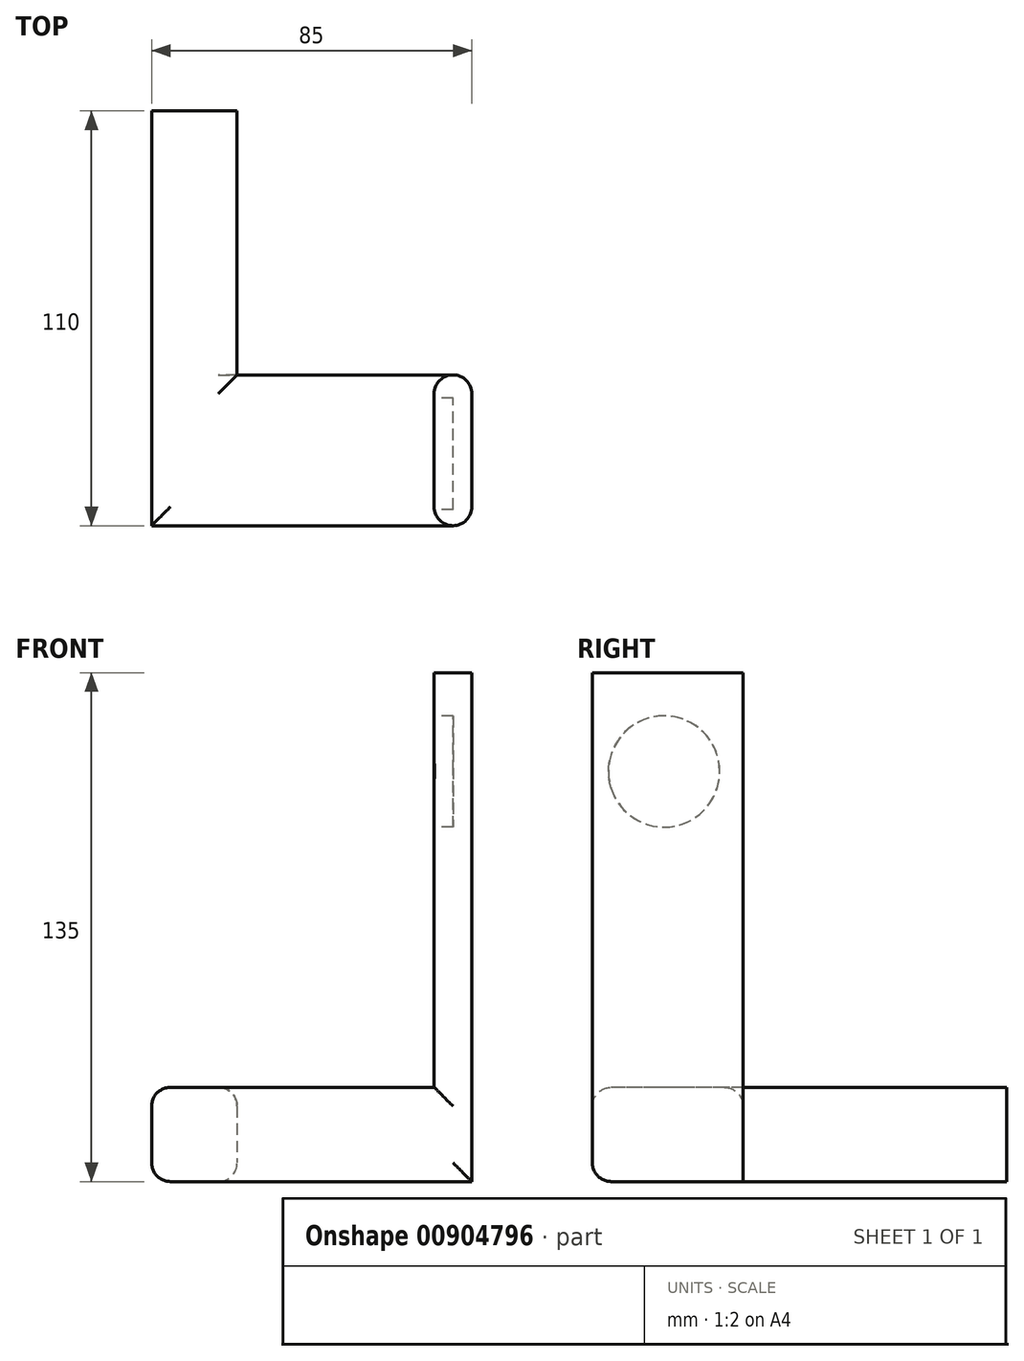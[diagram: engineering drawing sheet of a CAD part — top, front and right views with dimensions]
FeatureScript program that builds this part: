
annotation { "Feature Type Name" : "Feature", "Feature Type Description" : "" }
export const myFeature = defineFeature(function(context is Context, id is Id, definition is map)
    precondition{}
    {
        {
            var Q0;
            Q0=qCreatedBy(makeId("Top.planeOp"),FACE);
            var sketch = newSketch(context, id + "F0", { "sketchPlane" : qUnion([Q0])});
            skLineSegment(sketch, "E0", {"start": v(-68.8, 20.95) * mm, "end": v(16.2, 20.95) * mm});
            skLineSegment(sketch, "E1", {"start": v(16.2, 20.95) * mm, "end": v(16.2, -19.05) * mm});
            skLineSegment(sketch, "E2", {"start": v(16.2, -19.05) * mm, "end": v(-68.8, -19.05) * mm});
            skLineSegment(sketch, "E3", {"start": v(1.2, 20.95) * mm, "end": v(1.2, -19.05) * mm});
            skLineSegment(sketch, "E4", {"start": v(-68.8, 20.95) * mm, "end": v(-68.8, -19.05) * mm});
            skSolve(sketch);
        }
        {
            var Q0;
            {var subQ2=sQuery(id+"F0.wireOp",EDGE,"E3");Q0=makeQuery(id+"F0.imprint","IMPRINT",FACE,{"disambiguationData":[TD([[makeQuery(id+"F0.imprint","IMPRINT",EDGE,{"derivedFrom":subQ2}),-1.0]])]});}
            var Q1;
            {var subQ0=sQuery(id+"F0.wireOp",EDGE,"E1");Q1=makeQuery(id+"F0.imprint","IMPRINT",FACE,{"disambiguationData":[TD([[makeQuery(id+"F0.imprint","IMPRINT",EDGE,{"derivedFrom":subQ0}),-1.0]])]});}
            extrude(context, id + "F1", {"entities" : qUnion([Q0, Q1]), "depth" : 25 * mm, "offsetDistance" : 25 * mm});
        }
        {
            var Q0;
            Q0=makeQuery(id+"F1.opExtrude","CAP_FACE",FACE,{"disambiguationData":[OSD([sQuery(id+"F0.wireOp",EDGE,"E0"),sQuery(id+"F0.wireOp",EDGE,"E1"),sQuery(id+"F0.wireOp",EDGE,"E2"),sQuery(id+"F0.wireOp",EDGE,"E4")])],"isStart":false});
            var sketch = newSketch(context, id + "F2", { "sketchPlane" : qUnion([Q0])});
            skLineSegment(sketch, "E5", {"start": v(6.2, 20.95) * mm, "end": v(6.2, -19.05) * mm});
            skSolve(sketch);
        }
        {
            var Q0;
            {var subQ0=sQuery(id+"F2.wireOp",EDGE,"E5");Q0=makeQuery(id+"F2.imprint","IMPRINT",FACE,{"disambiguationData":[TD([[makeQuery(id+"F2.imprint","IMPRINT",EDGE,{"derivedFrom":subQ0}),1.0]])]});}
            extrude(context, id + "F3", {"entities" : qUnion([Q0]), "operationType" : NewBodyOperationType.ADD, "depth" : 110 * mm, "offsetDistance" : 25 * mm});
        }
        {
            var Q0;
            {var subQ0=sQuery(id+"F0.wireOp",EDGE,"E0");Q0=makeQuery(id+"F3.boolean.opBoolean","MERGE",FACE,{"derivedFrom":[makeQuery(id+"F1.opExtrude","SWEPT_FACE",FACE,{"disambiguationData":[OSD([subQ0])]}),makeQuery(id+"F3.opExtrude","SWEPT_FACE",FACE,{"disambiguationData":[OSD([subQ0])]})]});}
            var sketch = newSketch(context, id + "F4", { "sketchPlane" : qUnion([Q0])});
            skLineSegment(sketch, "E6.bottom", {"start": v(46.1, 25) * mm, "end": v(69.1, 25) * mm});
            skLineSegment(sketch, "E6.top", {"start": v(46.1, 0) * mm, "end": v(69.1, 0) * mm});
            skLineSegment(sketch, "E6.left", {"start": v(46.1, 25) * mm, "end": v(46.1, 0) * mm});
            skLineSegment(sketch, "E6.right", {"start": v(69.1, 25) * mm, "end": v(69.1, 0) * mm});
            skSolve(sketch);
        }
        {
            var Q0;
            {var subQ3=sQuery(id+"F4.wireOp",EDGE,"E6.left");Q0=makeQuery(id+"F4.imprint","IMPRINT",FACE,{"disambiguationData":[TD([[makeQuery(id+"F4.imprint","IMPRINT",EDGE,{"derivedFrom":subQ3}),1.0]])]});}
            extrude(context, id + "F5", {"entities" : qUnion([Q0]), "operationType" : NewBodyOperationType.ADD, "depth" : 70 * mm, "offsetDistance" : 25 * mm});
        }
        {
            var Q0;
            Q0=makeQuery(id+"F3.opExtrude","SWEPT_FACE",FACE,{"disambiguationData":[OSD([sQuery(id+"F2.wireOp",EDGE,"E5")])]});
            var sketch = newSketch(context, id + "F6", { "sketchPlane" : qUnion([Q0])});
            skCircle(sketch, "E7", {"center": v(0, 108.78) * mm, "radius": 14.75 * mm});
            skSolve(sketch);
        }
        {
            var Q0;
            Q0=makeQuery(id+"F6.imprint","IMPRINT",FACE,{"disambiguationData":[TD([[makeQuery(id+"F6.imprint","IMPRINT",EDGE,{"derivedFrom":sQuery(id+"F6.wireOp",EDGE,"E7")}),1.0]])]});
            extrude(context, id + "F7", {"entities" : qUnion([Q0]), "operationType" : NewBodyOperationType.REMOVE, "oppositeDirection" : true, "depth" : 5 * mm, "offsetDistance" : 25 * mm});
        }
        {
            var Q0;
            Q0=makeQuery(id+"F1.opExtrude","CAP_EDGE",EDGE,{"disambiguationData":[OSD([sQuery(id+"F0.wireOp",EDGE,"E2")])],"isStart":false});
            var Q1;
            Q1=makeQuery(id+"F1.opExtrude","CAP_EDGE",EDGE,{"disambiguationData":[OSD([sQuery(id+"F0.wireOp",EDGE,"E0")])],"isStart":false});
            var Q2;
            Q2=makeQuery(id+"F5.opExtrude","SWEPT_EDGE",EDGE,{"disambiguationData":[OSD([sQuery(id+"F0.wireOp",EDGE,"E0"),sQuery(id+"F4.wireOp",EDGE,"E6.bottom"),sQuery(id+"F4.wireOp",EDGE,"E6.left")])]});
            var Q3;
            {var subQ0=sQuery(id+"F0.wireOp",EDGE,"E4");Q3=makeQuery(id+"F5.boolean.opBoolean","MERGE",EDGE,{"derivedFrom":[makeQuery(id+"F1.opExtrude","CAP_EDGE",EDGE,{"disambiguationData":[OSD([subQ0])],"isStart":false}),makeQuery(id+"F5.opExtrude","SWEPT_EDGE",EDGE,{"disambiguationData":[OSD([sQuery(id+"F0.wireOp",EDGE,"E0"),subQ0,sQuery(id+"F4.wireOp",EDGE,"E6.bottom")])]})]});}
            var Q4;
            {var subQ0=sQuery(id+"F0.wireOp",EDGE,"E4");Q4=makeQuery(id+"F5.boolean.opBoolean","MERGE",EDGE,{"derivedFrom":[makeQuery(id+"F1.opExtrude","CAP_EDGE",EDGE,{"disambiguationData":[OSD([subQ0])],"isStart":true}),makeQuery(id+"F5.opExtrude","SWEPT_EDGE",EDGE,{"disambiguationData":[OSD([sQuery(id+"F0.wireOp",EDGE,"E0"),subQ0,sQuery(id+"F4.wireOp",EDGE,"E6.top")])]})]});}
            var Q5;
            Q5=makeQuery(id+"F1.opExtrude","CAP_EDGE",EDGE,{"disambiguationData":[OSD([sQuery(id+"F0.wireOp",EDGE,"E2")])],"isStart":true});
            var Q6;
            {var subQ0=sQuery(id+"F0.wireOp",EDGE,"E2");var subQ1=sQuery(id+"F0.wireOp",EDGE,"E1");Q6=makeQuery(id+"F3.boolean.opBoolean","MERGE",EDGE,{"derivedFrom":[makeQuery(id+"F1.opExtrude","SWEPT_EDGE",EDGE,{"disambiguationData":[OSD([subQ1,subQ0])]}),makeQuery(id+"F3.opExtrude","SWEPT_EDGE",EDGE,{"disambiguationData":[OSD([subQ1,subQ0])]})]});}
            var Q7;
            Q7=makeQuery(id+"F3.opExtrude","SWEPT_EDGE",EDGE,{"disambiguationData":[OSD([sQuery(id+"F0.wireOp",EDGE,"E2"),sQuery(id+"F2.wireOp",EDGE,"E5")])]});
            var Q8;
            {var subQ0=sQuery(id+"F0.wireOp",EDGE,"E1");var subQ1=sQuery(id+"F0.wireOp",EDGE,"E0");Q8=makeQuery(id+"F3.boolean.opBoolean","MERGE",EDGE,{"derivedFrom":[makeQuery(id+"F1.opExtrude","SWEPT_EDGE",EDGE,{"disambiguationData":[OSD([subQ1,subQ0])]}),makeQuery(id+"F3.opExtrude","SWEPT_EDGE",EDGE,{"disambiguationData":[OSD([subQ1,subQ0])]})]});}
            var Q9;
            Q9=makeQuery(id+"F3.opExtrude","SWEPT_EDGE",EDGE,{"disambiguationData":[OSD([sQuery(id+"F0.wireOp",EDGE,"E0"),sQuery(id+"F2.wireOp",EDGE,"E5")])]});
            var Q10;
            Q10=makeQuery(id+"F5.opExtrude","SWEPT_EDGE",EDGE,{"disambiguationData":[OSD([sQuery(id+"F0.wireOp",EDGE,"E0"),sQuery(id+"F4.wireOp",EDGE,"E6.top"),sQuery(id+"F4.wireOp",EDGE,"E6.left")])]});
            fillet(context, id + "F8", {"entities" : qUnion([Q0, Q1, Q2, Q3, Q4, Q5, Q6, Q7, Q8, Q9, Q10]), "radius" : 5 * mm, "tangentPropagation" : true, "allowEdgeOverflow" : false});
        }
    });
